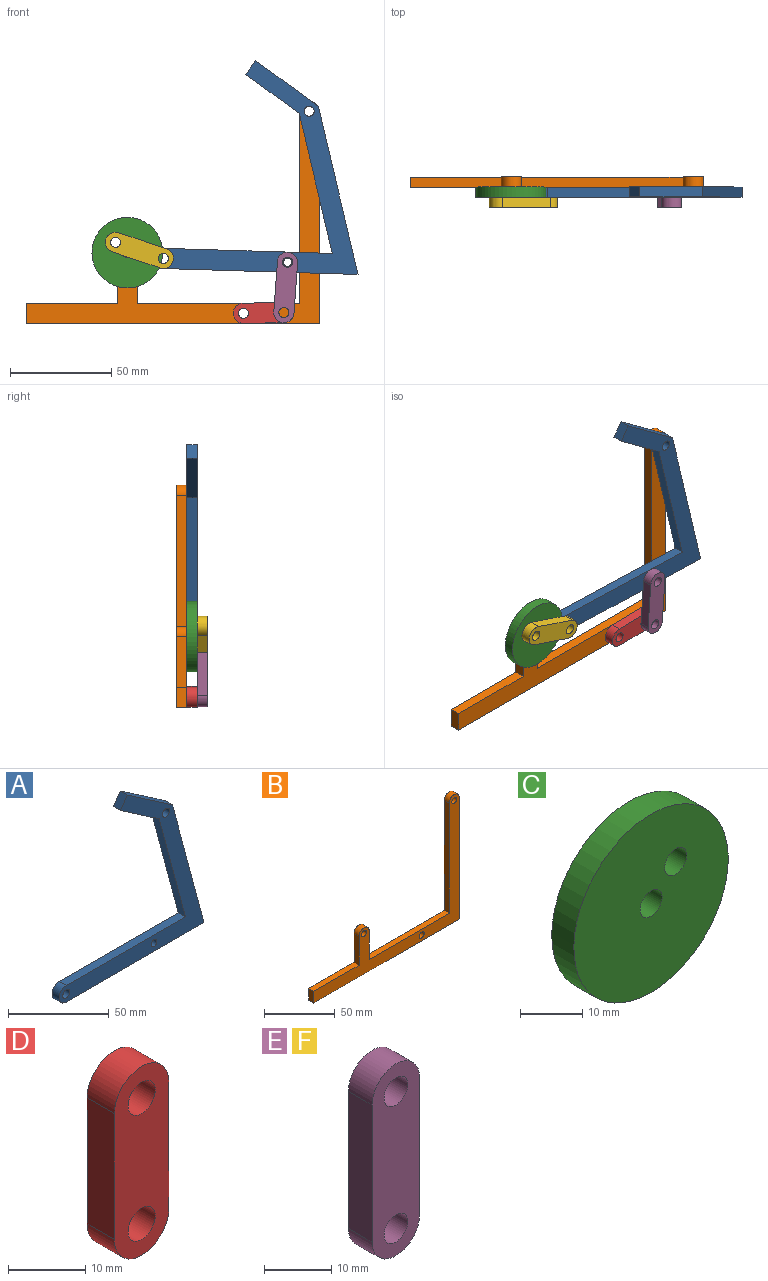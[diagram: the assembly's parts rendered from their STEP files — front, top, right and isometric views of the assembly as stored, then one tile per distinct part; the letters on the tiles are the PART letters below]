
ASSEMBLY  parts=6 mates=7
PART A: 13 faces, bbox 101.5x5x104.3 mm
  f0: plane 83.48x5mm, normal (0,0,1), area 417.4mm2, adj f1,f10,f11,f12
  f1: cylinder r=5mm len=10mm, axis (0,1,0), area 78.5mm2, adj f0,f2,f11,f12
  f2: plane 96.52x5mm, normal (0,0,-1), area 482.6mm2, adj f1,f3,f11,f12
  f3: plane 82.5x22.1mm, normal (0.97,0,0.26), area 427mm2, adj f2,f4,f11,f12
  f4: plane 31.69x21.77mm, normal (0.57,0,0.82), area 192.2mm2, adj f3,f5,f11,f12
  f5: plane 6.93x5mm, normal (-0.82,0,0.57), area 42.1mm2, adj f4,f6,f11,f12
  f6: plane 27.11x18.62mm, normal (-0.57,0,-0.82), area 164.5mm2, adj f5,f10,f11,f12
  f7: cylinder r=2.5mm len=5mm, axis (0,1,0), area 78.5mm2, adj f11,f12
  f8: cylinder r=2.5mm len=5mm, axis (0,1,0), area 78.5mm2, adj f11,f12
  f9: cylinder r=2.03mm len=5mm, axis (0,1,0), area 63.7mm2, adj f11,f12
  f10: plane 68.71x18.41mm, normal (-0.97,0,-0.26), area 355.6mm2, adj f0,f6,f11,f12
  f11: plane 104.26x101.52mm, normal (0,-1,0), area 1969.7mm2, adj f0,f1,f2,f3,f4,f5,f6,f7
  f12: plane 104.26x101.52mm, normal (0,1,0), area 1969.7mm2, adj f0,f1,f2,f3,f4,f5,f6,f7
PART B: 15 faces, bbox 145.2x5x110 mm
  f0: plane 95x5mm, normal (-1,0,0), area 475mm2, adj f1,f12,f13,f14
  f1: plane 80x5mm, normal (0,0,1), area 400mm2, adj f0,f2,f13,f14
  f2: plane 25x5mm, normal (1,0,0), area 125mm2, adj f1,f3,f13,f14
  f3: cylinder r=5mm len=10mm, axis (0,1,0), area 78.5mm2, adj f2,f4,f13,f14
  f4: plane 25x5mm, normal (-1,0,0), area 125mm2, adj f3,f5,f13,f14
  f5: plane 45.15x5mm, normal (0,0,1), area 225.8mm2, adj f4,f6,f13,f14
  f6: plane 10x5mm, normal (-1,0,0), area 50mm2, adj f5,f7,f13,f14
  f7: plane 145.15x5mm, normal (0,0,-1), area 725.8mm2, adj f6,f8,f13,f14
  f8: plane 105x5mm, normal (1,0,0), area 525mm2, adj f7,f12,f13,f14
  f9: cylinder r=2.5mm len=5mm, axis (0,1,0), area 78.5mm2, adj f13,f14
  f10: cylinder r=2.5mm len=5mm, axis (0,1,0), area 78.5mm2, adj f13,f14
  f11: cylinder r=2.5mm len=5mm, axis (0,1,0), area 78.5mm2, adj f13,f14
  f12: cylinder r=5mm len=10mm, axis (0,1,0), area 78.5mm2, adj f0,f8,f13,f14
  f13: plane 145.15x110mm, normal (0,-1,0), area 2671.2mm2, adj f0,f1,f2,f3,f4,f5,f6,f7
  f14: plane 145.15x110mm, normal (0,1,0), area 2671.2mm2, adj f0,f1,f2,f3,f4,f5,f6,f7
PART C: 5 faces, bbox 35x5x35 mm
  f0: cylinder r=2.5mm len=5mm, axis (0,1,0), area 78.5mm2, adj f3,f4
  f1: cylinder r=2.5mm len=5mm, axis (0,1,0), area 78.5mm2, adj f3,f4
  f2: cylinder r=17.5mm len=35mm, axis (0,1,0), area 549.8mm2, adj f3,f4
  f3: plane 35x35mm, normal (0,-1,0), area 922.8mm2, adj f0,f1,f2
  f4: plane 35x35mm, normal (0,1,0), area 922.8mm2, adj f0,f1,f2
PART D: 8 faces, bbox 10x5x30 mm
  f0: plane 20x5mm, normal (1,0,0), area 100mm2, adj f1,f4,f6,f7
  f1: cylinder r=5mm len=10mm, axis (0,1,0), area 78.5mm2, adj f0,f2,f6,f7
  f2: plane 20x5mm, normal (-1,0,0), area 100mm2, adj f1,f4,f6,f7
  f3: cylinder r=2.5mm len=5mm, axis (0,1,0), area 78.5mm2, adj f6,f7
  f4: cylinder r=5mm len=10mm, axis (0,1,0), area 78.5mm2, adj f0,f2,f6,f7
  f5: cylinder r=2.5mm len=5mm, axis (0,1,0), area 78.5mm2, adj f6,f7
  f6: plane 30x10mm, normal (0,-1,0), area 239.3mm2, adj f0,f1,f2,f3,f4,f5
  f7: plane 30x10mm, normal (0,1,0), area 239.3mm2, adj f0,f1,f2,f3,f4,f5
PART E: 8 faces, bbox 10x5x35 mm
  f0: plane 25x5mm, normal (1,0,0), area 125mm2, adj f1,f4,f6,f7
  f1: cylinder r=5mm len=10mm, axis (0,1,0), area 78.5mm2, adj f0,f2,f6,f7
  f2: plane 25x5mm, normal (-1,0,0), area 125mm2, adj f1,f4,f6,f7
  f3: cylinder r=2.5mm len=5mm, axis (0,1,0), area 78.5mm2, adj f6,f7
  f4: cylinder r=5mm len=10mm, axis (0,1,0), area 78.5mm2, adj f0,f2,f6,f7
  f5: cylinder r=2.5mm len=5mm, axis (0,1,0), area 78.5mm2, adj f6,f7
  f6: plane 35x10mm, normal (0,-1,0), area 289.3mm2, adj f0,f1,f2,f3,f4,f5
  f7: plane 35x10mm, normal (0,1,0), area 289.3mm2, adj f0,f1,f2,f3,f4,f5
PART F: same geometry as E
PLACE A rot(axis=(0,1,0),1.7deg) t=(26.95,-28.19,-13.49)mm
PLACE B t=(-50.09,-23.19,10.68)mm fixed
PLACE C rot(axis=(0,-1,0),94.6deg) t=(-80.87,-28.19,-7.92)mm
PLACE D rot(axis=(0,1,0),89deg) t=(-23.37,-28.19,-37.92)mm
PLACE E rot(axis=(0,1,0),4.1deg) t=(-3.37,-33.19,-37.57)mm
PLACE F rot(axis=(0,1,0),108.6deg) t=(-86.71,-33.19,-2.8)mm
MATE revolute E.f3 <-> D.f5  axis (0,1,0) through (-3.37,-33.19,-37.57)mm
MATE revolute D.f4 <-> B.f11  axis (0,1,0) through (-23.37,-28.19,-37.92)mm
MATE revolute C.f0 <-> B.f3  axis (0,1,0) through (-80.87,-28.19,-7.92)mm
MATE revolute E.f1 <-> A.f9  axis (0,1,0) through (-1.58,-33.19,-12.63)mm
MATE revolute F.f3 <-> C.f1  axis (0,1,0) through (-86.71,-33.19,-2.8)mm
MATE revolute A.f7 <-> B.f9  axis (0,1,0) through (9.13,-28.19,62.08)mm
MATE revolute F.f1 <-> A.f1  axis (0,1,0) through (-63.01,-33.19,-10.77)mm
